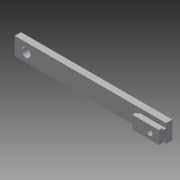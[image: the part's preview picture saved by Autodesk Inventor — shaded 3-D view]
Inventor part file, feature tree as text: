
AUTODESK INVENTOR PART (.ipt)
format: ipt  version: 2013 (Build 170138000, 138)  size: 110,080 bytes
history: native  units: in
note: dims shown in document units (in); Inventor stores cm internally (conversion verified against a paired STEP export)
features: extrude x5, sketch x5
ambient origin geometry x8: Origin, YZ Plane, XZ Plane, XY Plane, X Axis, Y Axis, Z Axis, Center Point
bodies: Solid1 (feature_tree)
feature tree (10):
  extrude  "Extrusion1"  Depth=1.0in
  extrude  "Extrusion2"  Depth=0.25in
  extrude  "Extrusion3"  Depth=0.2in TaperAngle=0.0deg
  extrude  "Extrusion4"  Depth=0.115in
  extrude  "Extrusion5"  Depth=0.35in
  sketch  "Sketch1"  dims[d0=8.5in d1=1.0in]
  sketch  "Sketch2"  dims[d2=0.35in d3=0.0in d4=0.25in]
  sketch  "Sketch3"  dims[d5=1.5in d6=0.2in d7=0.0in]
  sketch  "Sketch4"  dims[d8=0.115in d9=0.115in]
  sketch  "Sketch5"  dims[d10=0.2in d11=0.0in d12=0.35in d14=5.0in d15=0.0in d17=0.5in d18=1.0in d19=0.0in]
